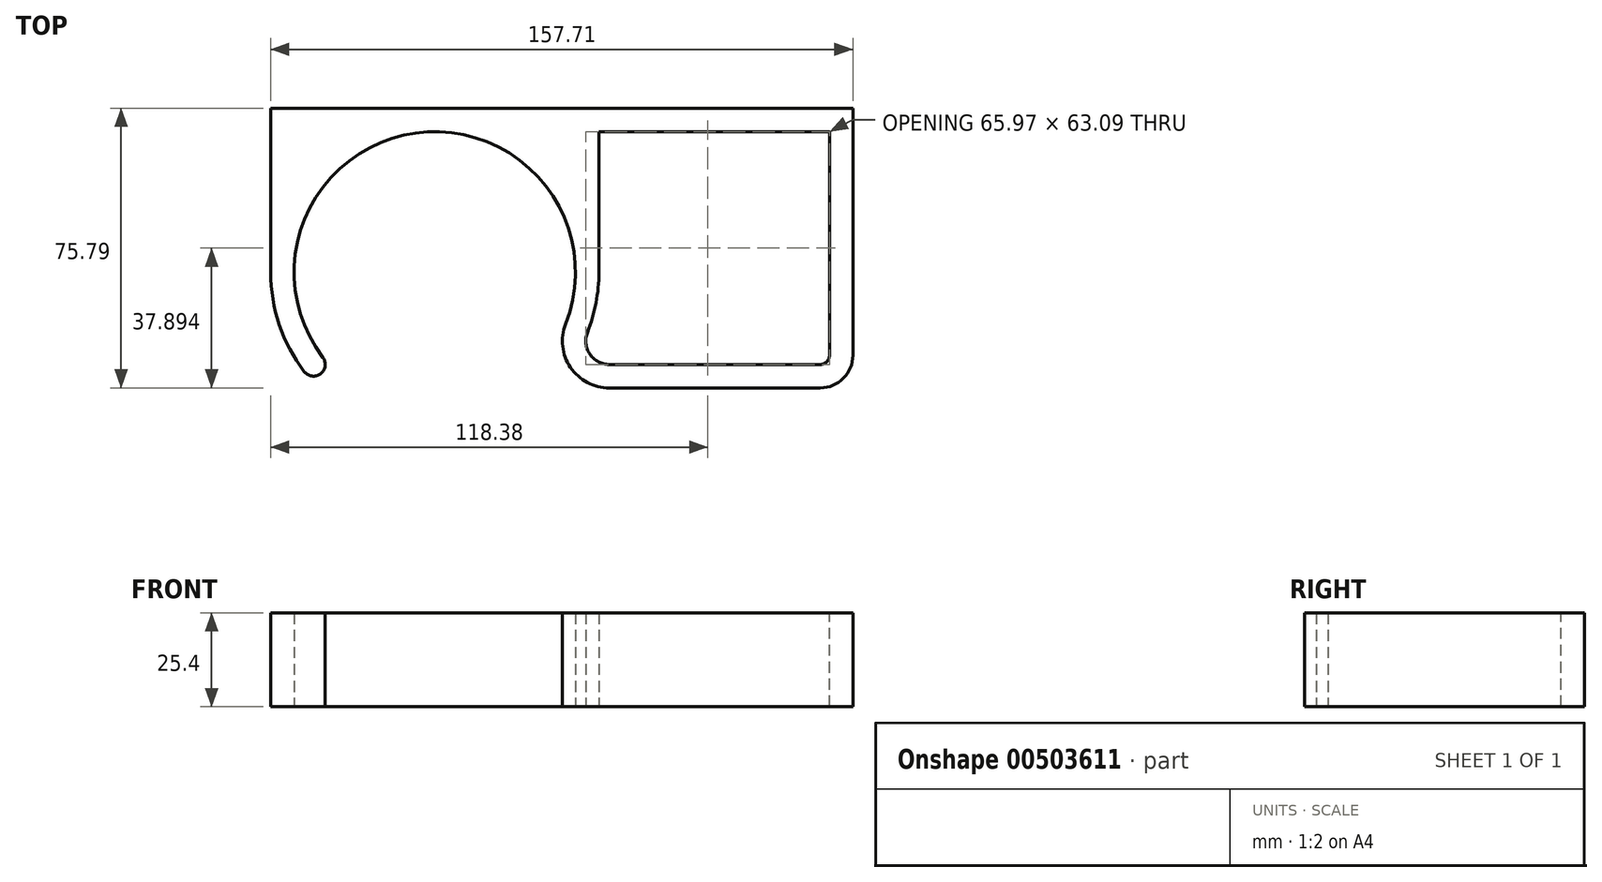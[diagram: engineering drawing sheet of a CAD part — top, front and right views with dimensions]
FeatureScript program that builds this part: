
annotation { "Feature Type Name" : "Feature", "Feature Type Description" : "" }
export const myFeature = defineFeature(function(context is Context, id is Id, definition is map)
    precondition{}
    {
        {
            var Q0;
            Q0=qCreatedBy(makeId("Top.planeOp"),FACE);
            var sketch = newSketch(context, id + "F0", { "sketchPlane" : qUnion([Q0])});
            skArc(sketch, "E0", {"start": v(35.44, -13.98) * mm, "mid": v(0.13, 38.1) * mm, "end": v(-35.53, -13.75) * mm});
            skArc(sketch, "E1.0", {"start": v(41.35, -16.31) * mm, "mid": v(0, 44.45) * mm, "end": v(-41.35, -16.31) * mm});
            skArc(sketch, "E2", {"start": v(41.35, -16.31) * mm, "mid": v(42, -22.21) * mm, "end": v(47.26, -25) * mm});
            skArc(sketch, "E3.0", {"start": v(35.44, -13.98) * mm, "mid": v(36.76, -25.79) * mm, "end": v(47.26, -31.34) * mm});
            skLineSegment(sketch, "E4", {"start": v(47.26, -25) * mm, "end": v(104.4, -25) * mm});
            skLineSegment(sketch, "E5", {"start": v(47.26, -31.34) * mm, "end": v(104.4, -31.34) * mm});
            skPoint(sketch, "E6.orphan", {"position": v(53.16, -16.31) * mm});
            skArc(sketch, "E7", {"start": v(104.4, -25) * mm, "mid": v(106.18, -24.26) * mm, "end": v(106.91, -22.48) * mm});
            skArc(sketch, "E8.0", {"start": v(104.4, -31.34) * mm, "mid": v(110.67, -28.75) * mm, "end": v(113.26, -22.48) * mm});
            skLineSegment(sketch, "E9", {"start": v(113.26, -22.48) * mm, "end": v(113.26, 44.45) * mm});
            skLineSegment(sketch, "E10", {"start": v(106.91, -22.48) * mm, "end": v(106.91, 44.45) * mm});
            skPoint(sketch, "E11.orphan", {"position": v(104.4, -19.97) * mm});
            skPoint(sketch, "E12.startSnap0", {"position": v(0, 44.45) * mm});
            skArc(sketch, "E13", {"start": v(-35.53, -13.75) * mm, "mid": v(-33.26, -18.58) * mm, "end": v(-30.34, -23.05) * mm});
            skArc(sketch, "E14.0", {"start": v(-41.46, -16.04) * mm, "mid": v(-38.8, -21.68) * mm, "end": v(-35.4, -26.9) * mm});
            skArc(sketch, "E15", {"start": v(-35.4, -26.9) * mm, "mid": v(-30.94, -27.5) * mm, "end": v(-30.34, -23.05) * mm});
            skLineSegment(sketch, "E16", {"start": v(-44.45, 44.45) * mm, "end": v(-44.45, 0) * mm});
            skLineSegment(sketch, "E17", {"start": v(0, 0) * mm, "end": v(0, 86.71) * mm, "construction": true});
            skLineSegment(sketch, "E18.MirrorCS", {"start": v(44.45, 44.45) * mm, "end": v(44.45, 0) * mm});
            skLineSegment(sketch, "E19", {"start": v(-44.45, 44.45) * mm, "end": v(113.26, 44.45) * mm});
            skSolve(sketch);
        }
        {
            var Q0;
            Q0=makeQuery(id+"F0.imprint","IMPRINT",FACE,{"disambiguationData":[TD([[makeQuery(id+"F0.imprint","IMPRINT",EDGE,{"derivedFrom":sQuery(id+"F0.wireOp",EDGE,"E0")}),-1.0]])]});
            extrude(context, id + "F1", {"entities" : qUnion([Q0]), "endBound" : BoundingType.SYMMETRIC, "depth" : 25.4 * mm});
        }
        {
            var Q0;
            {var subQ3=sQuery(id+"F0.wireOp",EDGE,"E18.MirrorCS");Q0=makeQuery(id+"F0.imprint","IMPRINT",FACE,{"disambiguationData":[TD([[makeQuery(id+"F0.imprint","IMPRINT",EDGE,{"derivedFrom":subQ3}),-1.0]])]});}
            var Q1;
            {var subQ0=sQuery(id+"F0.wireOp",EDGE,"2teKiRBU-1FJx-mVyY-VFxI-G9wrVXuZ8vhX");Q1=makeQuery(id+"F0.imprint","IMPRINT",FACE,{"disambiguationData":[TD([[makeQuery(id+"F0.imprint","IMPRINT",EDGE,{"derivedFrom":subQ0}),1.0]])]});}
            extrude(context, id + "F2", {"entities" : qUnion([Q0, Q1]), "operationType" : NewBodyOperationType.ADD, "endBound" : BoundingType.SYMMETRIC, "depth" : 25.4 * mm, "offsetDistance" : 25.4 * mm});
        }
        {
            var Q0;
            {var subQ0=sQuery(id+"F0.wireOp",EDGE,"E16");Q0=makeQuery(id+"F0.imprint","IMPRINT",FACE,{"disambiguationData":[TD([[makeQuery(id+"F0.imprint","IMPRINT",EDGE,{"derivedFrom":subQ0}),1.0]])]});}
            extrude(context, id + "F3", {"entities" : qUnion([Q0]), "operationType" : NewBodyOperationType.ADD, "endBound" : BoundingType.SYMMETRIC, "depth" : 25.4 * mm, "offsetDistance" : 25.4 * mm});
        }
        {
            var Q0;
            Q0=makeQuery(id+"F1.opExtrude","SWEPT_FACE",FACE,{"disambiguationData":[OSD([sQuery(id+"F0.wireOp",EDGE,"E10")])]});
            var sketch = newSketch(context, id + "F4", { "sketchPlane" : qUnion([Q0])});
            skLineSegment(sketch, "E20.bottom", {"start": v(-44.45, -12.7) * mm, "end": v(-38.1, -12.7) * mm});
            skLineSegment(sketch, "E20.top", {"start": v(-44.45, 12.7) * mm, "end": v(-38.1, 12.7) * mm});
            skLineSegment(sketch, "E20.left", {"start": v(-44.45, -12.7) * mm, "end": v(-44.45, 12.7) * mm});
            skLineSegment(sketch, "E20.right", {"start": v(-38.1, -12.7) * mm, "end": v(-38.1, 12.7) * mm});
            skSolve(sketch);
        }
        {
            var Q0;
            Q0=makeQuery(id+"F4.imprint","IMPRINT",FACE,{"disambiguationData":[TD([[makeQuery(id+"F4.imprint","IMPRINT",EDGE,{"derivedFrom":sQuery(id+"F4.wireOp",EDGE,"E20.bottom")}),-1.0]])]});
            extrude(context, id + "F5", {"entities" : qUnion([Q0]), "operationType" : NewBodyOperationType.ADD, "endBound" : BoundingType.UP_TO_NEXT, "depth" : 25.4 * mm, "offsetDistance" : 25.4 * mm});
        }
    });
